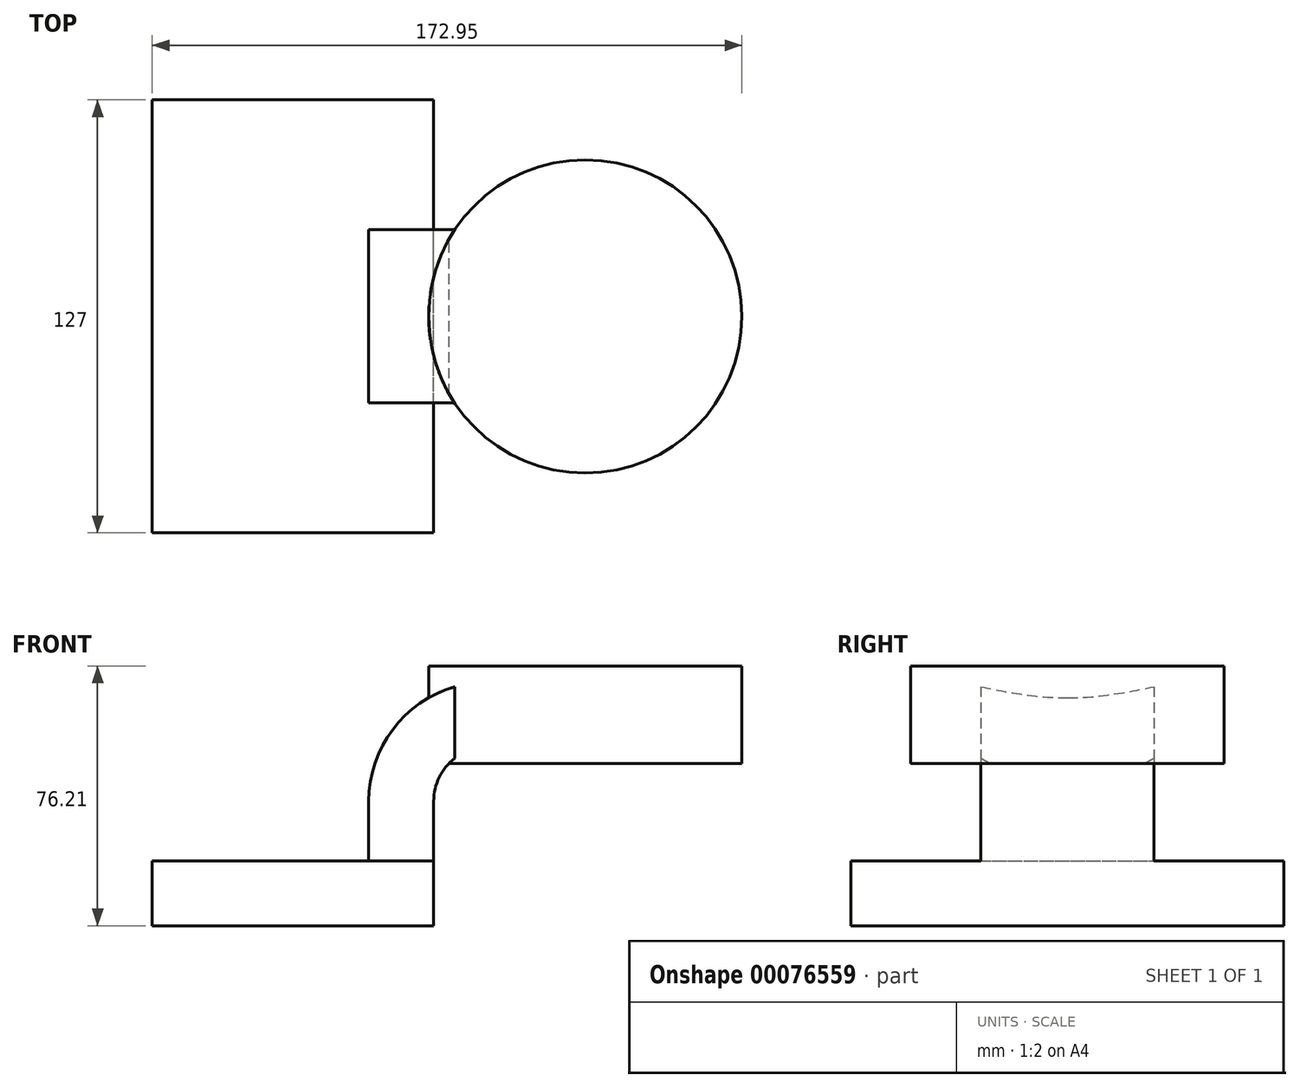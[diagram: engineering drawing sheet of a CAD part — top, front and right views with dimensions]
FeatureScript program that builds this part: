
annotation { "Feature Type Name" : "Feature", "Feature Type Description" : "" }
export const myFeature = defineFeature(function(context is Context, id is Id, definition is map)
    precondition{}
    {
        {
            var Q0;
            Q0=qCreatedBy(makeId("Front.planeOp"),FACE);
            var sketch = newSketch(context, id + "F0", { "sketchPlane" : qUnion([Q0])});
            skLineSegment(sketch, "E0.bottom", {"start": v(-41.28, -9.53) * mm, "end": v(41.28, -9.53) * mm});
            skLineSegment(sketch, "E0.top", {"start": v(-41.28, 9.52) * mm, "end": v(41.28, 9.52) * mm});
            skLineSegment(sketch, "E0.left", {"start": v(-41.28, -9.53) * mm, "end": v(-41.28, 9.52) * mm});
            skLineSegment(sketch, "E0.right", {"start": v(41.28, -9.53) * mm, "end": v(41.28, 9.52) * mm});
            skPoint(sketch, "E0.middle", {"position": v(0, 0) * mm});
            skLineSegment(sketch, "E1.bottom", {"start": v(80.87, 38.1) * mm, "end": v(131.67, 38.1) * mm});
            skLineSegment(sketch, "E1.top", {"start": v(80.87, 66.67) * mm, "end": v(131.67, 66.67) * mm});
            skLineSegment(sketch, "E1.left", {"start": v(80.87, 38.1) * mm, "end": v(80.87, 66.67) * mm});
            skLineSegment(sketch, "E1.right", {"start": v(131.67, 38.1) * mm, "end": v(131.67, 66.67) * mm});
            skPoint(sketch, "E1.middle", {"position": v(106.27, 52.39) * mm});
            skLineSegment(sketch, "E2", {"start": v(41.27, 9.52) * mm, "end": v(41.27, 27) * mm});
            skArc(sketch, "E3", {"start": v(41.27, 27) * mm, "mid": v(45.92, 38.23) * mm, "end": v(57.15, 42.88) * mm});
            skLineSegment(sketch, "E4", {"start": v(57.15, 42.88) * mm, "end": v(85.73, 42.88) * mm});
            skLineSegment(sketch, "E5.0", {"start": v(57.15, 61.93) * mm, "end": v(85.73, 61.93) * mm});
            skArc(sketch, "E5.1", {"start": v(22.22, 27) * mm, "mid": v(32.45, 51.7) * mm, "end": v(57.15, 61.93) * mm});
            skLineSegment(sketch, "E5.2", {"start": v(22.22, 9.52) * mm, "end": v(22.22, 27) * mm});
            skLineSegment(sketch, "E6", {"start": v(85.73, 38.1) * mm, "end": v(85.73, 66.67) * mm});
            skFitSpline(sketch, "E7", {"points": [v(-41.28, 9.53) * mm, v(57.15, 61.93) * mm], "startDerivative": vector(0, 67.1) * mm, "endDerivative": vector(125.8, 0) * mm});
            skSolve(sketch);
        }
        {
            var Q0;
            Q0=makeQuery(id+"F0.imprint","IMPRINT",FACE,{"disambiguationData":[TD([[makeQuery(id+"F0.imprint","IMPRINT",EDGE,{"derivedFrom":sQuery(id+"F0.wireOp",EDGE,"E0.bottom")}),1.0]])]});
            extrude(context, id + "F1", {"entities" : qUnion([Q0]), "endBound" : BoundingType.SYMMETRIC, "depth" : 127 * mm});
        }
        {
            var Q0;
            {var subQ1=sQuery(id+"F0.wireOp",EDGE,"E2");Q0=makeQuery(id+"F0.imprint","IMPRINT",FACE,{"disambiguationData":[TD([[makeQuery(id+"F0.imprint","IMPRINT",EDGE,{"derivedFrom":subQ1}),1.0]])]});}
            var Q1;
            {var subQ0=sQuery(id+"F0.wireOp",EDGE,"E4");var subQ1=sQuery(id+"F0.wireOp",EDGE,"E1.left");var subQ2=makeQuery(id+"F0.imprint","INTERSECT",VERTEX,{"derivedFrom":[subQ1,subQ0]});Q1=makeQuery(id+"F0.imprint","IMPRINT",FACE,{"disambiguationData":[TD([[makeQuery(id+"F0.imprint","IMPRINT",EDGE,{"disambiguationData":[TD([[subQ2,-1.0]])],"derivedFrom":subQ1}),-1.0]])]});}
            extrude(context, id + "F2", {"entities" : qUnion([Q0, Q1]), "operationType" : NewBodyOperationType.ADD, "endBound" : BoundingType.SYMMETRIC, "depth" : 50.8 * mm});
        }
        {
            var Q0;
            Q0=makeQuery(id+"F0.imprint","IMPRINT",FACE,{"disambiguationData":[TD([[makeQuery(id+"F0.imprint","IMPRINT",EDGE,{"derivedFrom":sQuery(id+"F0.wireOp",EDGE,"E5.1")}),1.0]])]});
            extrude(context, id + "F3", {"entities" : qUnion([Q0]), "operationType" : NewBodyOperationType.ADD, "endBound" : BoundingType.SYMMETRIC, "depth" : 15.88 * mm});
        }
        {
            var Q0;
            {var subQ0=sQuery(id+"F0.wireOp",EDGE,"E1.right");Q0=makeQuery(id+"F0.imprint","IMPRINT",FACE,{"disambiguationData":[TD([[makeQuery(id+"F0.imprint","IMPRINT",EDGE,{"derivedFrom":subQ0}),1.0]])]});}
            var Q1;
            Q1=sQuery(id+"F0.wireOp",EDGE,"E6");
            revolve(context, id + "F4", {"operationType" : NewBodyOperationType.ADD, "entities" : qUnion([Q0]), "axis" : qUnion([Q1]), "revolveType" : RevolveType.FULL});
        }
    });
